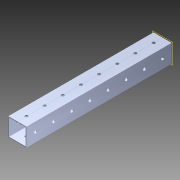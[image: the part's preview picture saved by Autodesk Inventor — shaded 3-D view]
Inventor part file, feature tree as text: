
AUTODESK INVENTOR PART (.ipt)
format: ipt  version: 2014 (Build 180170000, 170)  size: 1,150,464 bytes
history: native  units: in
note: dims shown in document units (in); Inventor stores cm internally (conversion verified against a paired STEP export)
features: pattern_circular x1, other x1, plane x1, extrude x1, imported_body x1, sketch x1
ambient origin geometry x8: Origin, YZ Plane, XZ Plane, XY Plane, X Axis, Y Axis, Z Axis, Center Point
bodies: Body1 (feature_tree)
feature tree (6):
  pattern_circular  "CirPattern2"
  other  "217-3426-STEP1"
  plane  "Work Plane1"
  extrude  "Extrusion1"  Depth=3937.0079in TaperAngle=0.0deg
  imported_body  "Base1"
  sketch  "Sketch1"  dims[d0=-8.0in d1=3937.0079in d2=0.0in]
